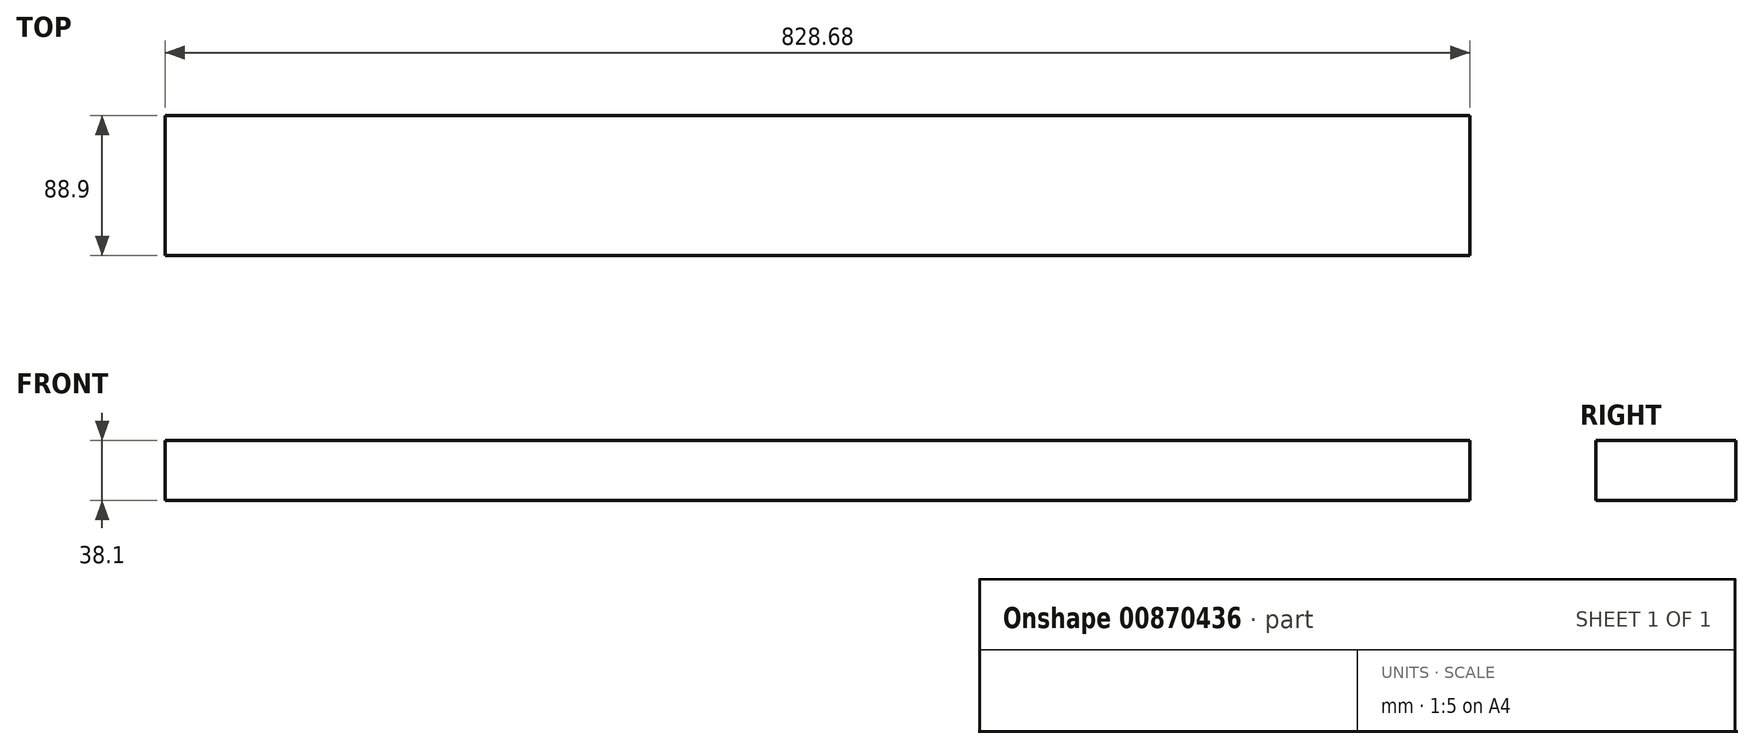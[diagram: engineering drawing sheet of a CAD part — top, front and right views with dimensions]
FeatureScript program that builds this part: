
annotation { "Feature Type Name" : "Feature", "Feature Type Description" : "" }
export const myFeature = defineFeature(function(context is Context, id is Id, definition is map)
    precondition{}
    {
        {
            var Q0;
            Q0=qCreatedBy(makeId("Right.planeOp"),FACE);
            var sketch = newSketch(context, id + "F0", { "sketchPlane" : qUnion([Q0])});
            skLineSegment(sketch, "E0.bottom", {"start": v(46.26, 19.05) * mm, "end": v(-42.64, 19.05) * mm});
            skLineSegment(sketch, "E0.top", {"start": v(46.26, -19.05) * mm, "end": v(-42.64, -19.05) * mm});
            skLineSegment(sketch, "E0.left", {"start": v(46.26, 19.05) * mm, "end": v(46.26, -19.05) * mm});
            skLineSegment(sketch, "E0.right", {"start": v(-42.64, 19.05) * mm, "end": v(-42.64, -19.05) * mm});
            skPoint(sketch, "E0.middle", {"position": v(1.8, 0) * mm});
            skSolve(sketch);
        }
        {
            var Q0;
            Q0=makeQuery(id+"F0.imprint","IMPRINT",FACE,{"disambiguationData":[TD([[makeQuery(id+"F0.imprint","IMPRINT",EDGE,{"derivedFrom":sQuery(id+"F0.wireOp",EDGE,"E0.bottom")}),1.0]])]});
            extrude(context, id + "F1", {"entities" : qUnion([Q0]), "depth" : 828.67 * mm, "offsetDistance" : 25.4 * mm});
        }
    });
